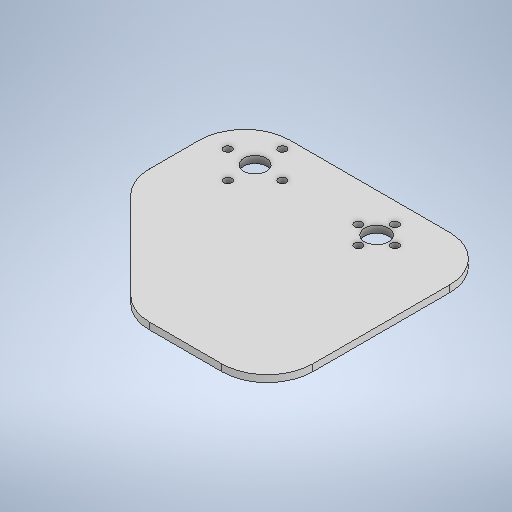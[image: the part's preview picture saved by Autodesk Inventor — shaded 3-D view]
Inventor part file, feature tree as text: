
AUTODESK INVENTOR PART (.ipt)
format: ipt  version: 2025.2 (Build 292293000, 293)  size: 267,264 bytes
history: native  units: mm
features: sketch x4, extrude x2, fillet x1
ambient origin geometry x8: Origin, YZ Plane, XZ Plane, XY Plane, X Axis, Y Axis, Z Axis, Center Point
bodies: Solid1 (feature_tree)
feature tree (7):
  extrude  "Extrusion1"  Depth=50.0mm
  extrude  "Extrusion6"  Depth=3.0mm
  fillet  "Fillet1"  Radius=10.5mm
  sketch  "Sketch1"  dims[d0=150.0mm d1=50.0mm]
  sketch  "Sketch6"  dims[d43=10.0mm d44=3.5mm d45=40.0mm d47=360.0deg d49=24.0mm d50=3.5mm d51=40.0mm d53=360.0deg d55=0.0mm d56=0.0mm d57=40.0mm d58=50.0mm d59=50.0mm d60=60.0mm d61=20.0mm d26=0.5mm d27=0.872665mm d28=0.5mm d29=0.872665mm]
  sketch  "Sketch Circular Pattern1"  dims[d2=3.0mm d3=0.0mm d40=17.0mm d41=10.5mm]
  sketch  "Sketch Circular Pattern2"  dims[d42=53.4mm]
